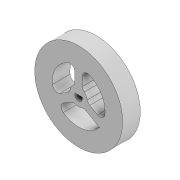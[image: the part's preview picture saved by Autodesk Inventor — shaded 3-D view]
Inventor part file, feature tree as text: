
AUTODESK INVENTOR PART (.ipt)
format: ipt  version: 2022 (Build 260153000, 153)  size: 151,040 bytes
history: native  units: mm
features: extrude x4, sketch x4, fillet x1
ambient origin geometry x8: Origin, YZ Plane, XZ Plane, XY Plane, X Axis, Y Axis, Z Axis, Center Point
bodies: Solid1 (feature_tree)
feature tree (9):
  extrude  "Extrusion1"  Depth=7.0mm TaperAngle=0.0deg
  extrude  "Extrusion2"  Depth=7.0mm
  fillet  "Fillet1"  Radius=3.0mm
  extrude  "Extrusion4"  TaperAngle=0.0deg  [1 undecoded]
  extrude  "Extrusion3"  TaperAngle=0.0deg  [1 undecoded]
  sketch  "Sketch1"  dims[d0=35.0mm d1=7.0mm d2=0.0mm]
  sketch  "Sketch2"  dims[d3=21.0mm d4=7.0mm d5=3.0mm]
  sketch  "Sketch3"  dims[d6=30.0mm d8=360.0deg d10=0.0mm d11=0.0mm]
  sketch  "Sketch4"  dims[d12=2.0mm d15=0.0mm d16=0.0mm d17=3.0mm d19=2.0mm d20=2.0mm d21=0.0mm]
note: 2 required parameter values undecoded (feature->parameter linkage not recoverable at this tier; creation-order binding heuristic only, values carry confidence <= 0.55)
